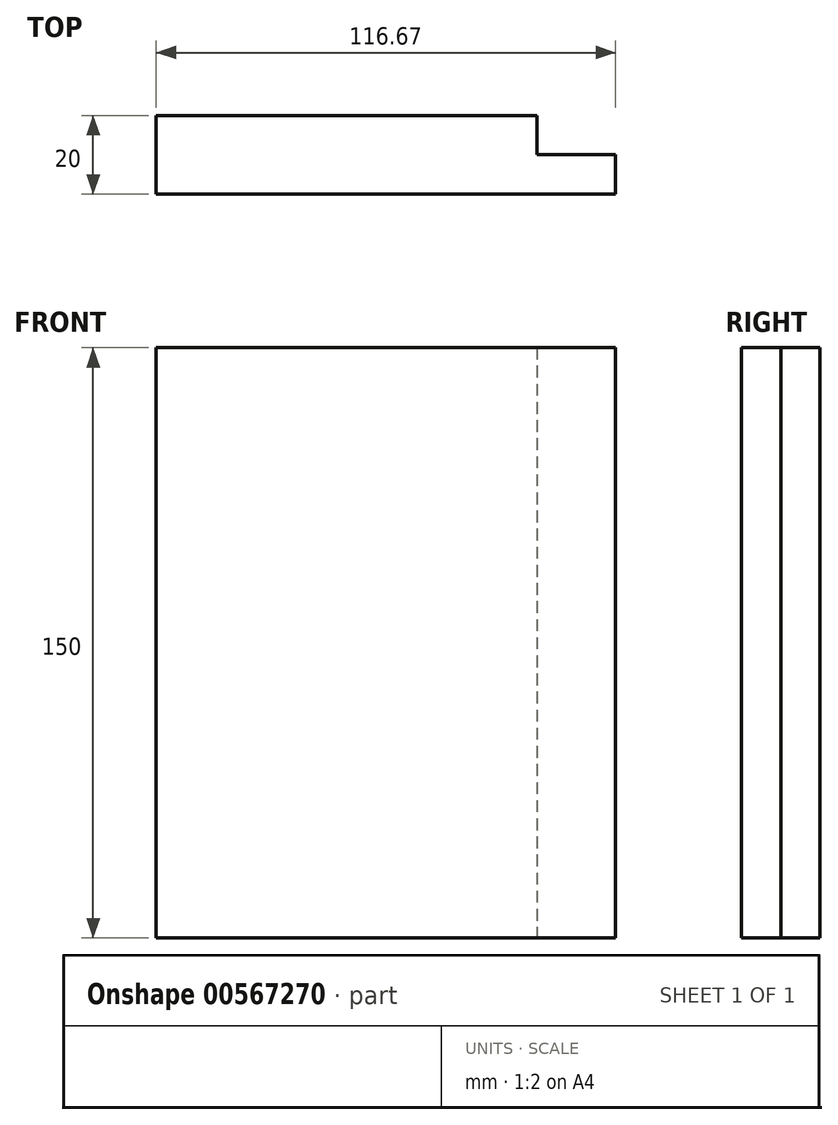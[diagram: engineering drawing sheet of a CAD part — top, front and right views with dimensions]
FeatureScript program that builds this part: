
annotation { "Feature Type Name" : "Feature", "Feature Type Description" : "" }
export const myFeature = defineFeature(function(context is Context, id is Id, definition is map)
    precondition{}
    {
        {
            var Q0;
            Q0=qCreatedBy(makeId("Front.planeOp"),FACE);
            var sketch = newSketch(context, id + "F0", { "sketchPlane" : qUnion([Q0])});
            skLineSegment(sketch, "E0.bottom", {"start": v(0, 0) * mm, "end": v(-116.67, 0) * mm});
            skLineSegment(sketch, "E0.top", {"start": v(0, 150) * mm, "end": v(-116.67, 150) * mm});
            skLineSegment(sketch, "E0.left", {"start": v(0, 0) * mm, "end": v(0, 150) * mm});
            skLineSegment(sketch, "E0.right", {"start": v(-116.67, 0) * mm, "end": v(-116.67, 150) * mm});
            skLineSegment(sketch, "E1.bottom", {"start": v(-58.33, 0) * mm, "end": v(-58.33, 0) * mm});
            skLineSegment(sketch, "E1.top", {"start": v(-58.33, 150) * mm, "end": v(-58.33, 150) * mm});
            skLineSegment(sketch, "E2", {"start": v(-104.66, 150) * mm, "end": v(-104.66, 0) * mm});
            skSolve(sketch);
        }
        {
            var Q0;
            Q0 = qSketchRegion(id + "F0", true);
            extrude(context, id + "F1", {"entities" : qUnion([Q0]), "depth" : 20 * mm, "offsetDistance" : 25.4 * mm});
        }
        {
            var Q0;
            Q0=makeQuery(id+"F1.opExtrude","SWEPT_FACE",FACE,{"disambiguationData":[OSD([sQuery(id+"F0.wireOp",EDGE,"E0.bottom")])]});
            var sketch = newSketch(context, id + "F2", { "sketchPlane" : qUnion([Q0])});
            skLineSegment(sketch, "E3", {"start": v(0, 10) * mm, "end": v(-20, 10) * mm});
            skLineSegment(sketch, "E4", {"start": v(-20, 10) * mm, "end": v(-20, 0) * mm});
            skSolve(sketch);
        }
        {
            var Q0;
            {var subQ0=sQuery(id+"F2.wireOp",EDGE,"E3");Q0=makeQuery(id+"F2.imprint","IMPRINT",FACE,{"disambiguationData":[TD([[makeQuery(id+"F2.imprint","IMPRINT",EDGE,{"derivedFrom":subQ0}),1.0]])]});}
            extrude(context, id + "F3", {"entities" : qUnion([Q0]), "operationType" : NewBodyOperationType.REMOVE, "oppositeDirection" : true, "depth" : 180 * mm, "offsetDistance" : 25.4 * mm});
        }
    });
